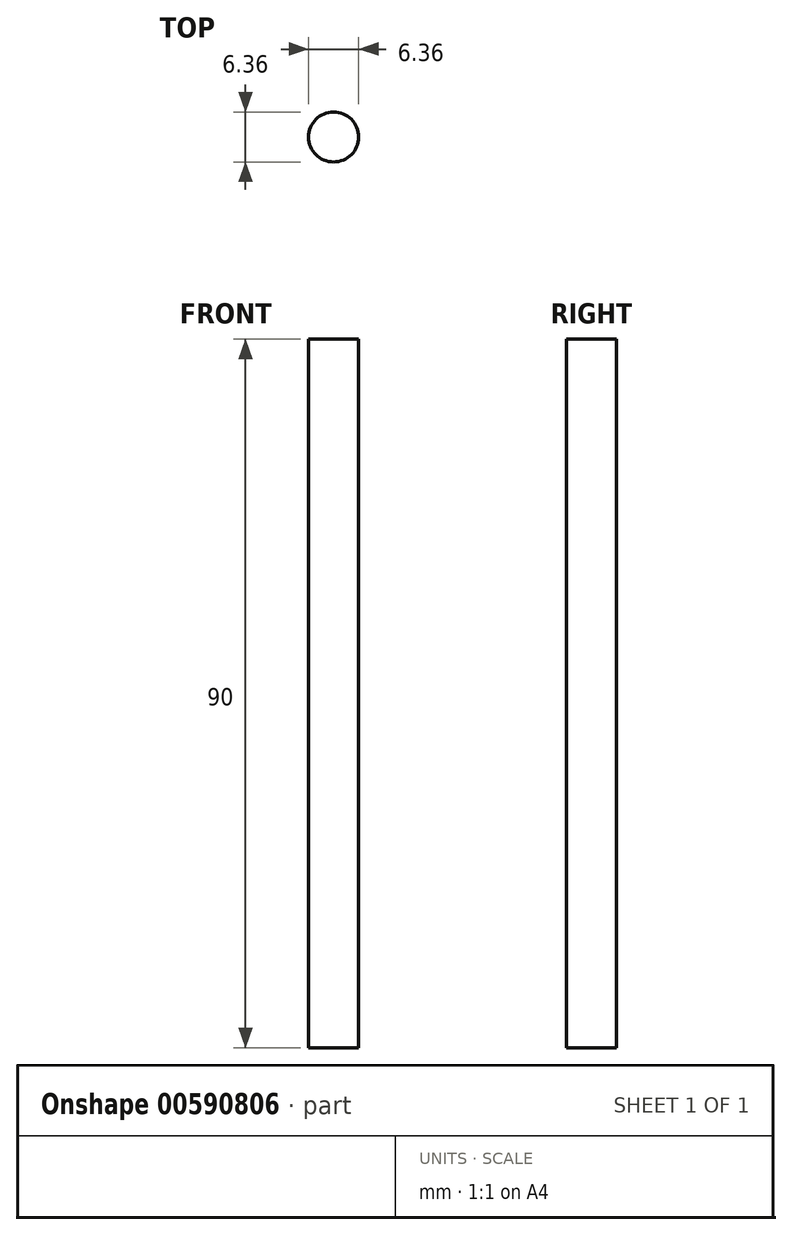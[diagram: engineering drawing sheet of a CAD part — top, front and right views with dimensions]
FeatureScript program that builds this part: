
annotation { "Feature Type Name" : "Feature", "Feature Type Description" : "" }
export const myFeature = defineFeature(function(context is Context, id is Id, definition is map)
    precondition{}
    {
        {
            var Q0;
            Q0=qCreatedBy(makeId("Top.planeOp"),FACE);
            var sketch = newSketch(context, id + "F0", { "sketchPlane" : qUnion([Q0])});
            skCircle(sketch, "E0", {"center": v(0, 0) * mm, "radius": 3.18 * mm});
            skSolve(sketch);
        }
        {
            var Q0;
            Q0=sQuery(id+"F0.wireOp",EDGE,"E0");
            extrude(context, id + "F1", {"bodyType" : ToolBodyType.SURFACE, "surfaceEntities" : qUnion([Q0]), "depth" : 90 * mm, "offsetDistance" : 25 * mm});
        }
    });
